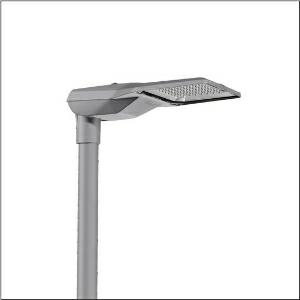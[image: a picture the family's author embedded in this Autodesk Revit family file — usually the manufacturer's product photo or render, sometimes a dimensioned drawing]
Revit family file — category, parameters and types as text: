
# Revit family: streetlight_sl_21_midi___pc-l_5xe3f33s08mb_4952
name_source: partatom
category: Lighting Fixtures
units: mm (PartAtom-declared; Revit-internal decimal feet)

## family parameters
Cut with Voids When Loaded = No
Host = Face
Light Source = No
Part Type = Normal
Room Calculation Point = No
Round Connector Dimension = Use Diameter
Shared = No

## types (1)
- --- (1 x LED, 17390 lm, 136 W, 3000K)
    Apparent Load = 136 VA
    CIE Flux Codes = 38 78 98 100 100
    Color Rendering = 70
    Color Temperature = 3000K
    Default Elevation = 1800 mm
    Description = Streetlight SL 21 midi, mast luminaire, primary light control with lens, of PMMA, primary optical cover: cover, of toughened safety glass, transparent, light distribution: PC-L, light emission: direct distribution, primary light characteristic: asymmetric, left, installation type: side-entry, post-top, LED, High Power LED, rated luminous flux: 17.390lm, luminous efficacy: 128lm/W, light colour: 730, colour temperature: 3000K, control gear: D4i, control: overheat protection, constant luminous flux control, time-dependent luminous flux control, flexible luminous flux parameterisation, pre-setting: logarithmic dimming characteristic, mains connection: 230..240V, AC, 50/60Hz, start of lifetime: 136W, end of service life: 142W, reduction: 61W, luminaire housing, of diecast aluminium, powder-coated, SITECO metallic grey (DB 702S), corrosivity category C5 high according to DIN EN ISO 12944, please order mast flange separately, inclination adjustable: 0°, 5°, 10°, 15°, sealing non-destructively replaceable, multi-level sealing system, length: 644mm, width: 335mm, height: 110mm, mast flange for spigot size: 42mm (side-entry): 5XC10008XM4, 60/48mm (side-entry/post-top): 5XC10108XM2, 76/60mm (side-entry/post-top): 5XC10108XM1, mounting height: 4..8m, Smart Interface above, protection rating (complete): IP66, insulation class (complete): insulation class II (safety insulation), certification: CE, ENEC, ENEC+, VDE, impact resistance: IK10, permissible operating ambient temperature for outdoor applications: -40..+50°C, standard-compliant lighting for roads and squares, packaging unit: 1 piece

Light Distribution: PC-L
    Height = 111 mm
    Lamp = 1 x LED
    Lamp Light Flux = 17390 lm
    Lamp Power = 136 W
    Lamp count = 1
    Length = 644 mm
    Luminous efficacy = 128 lm/W
    Manufacturer = Siteco
    ModVariant = No
    Model = 5XE3F33S08MB
    Number of Poles = 1
    OnlyDefault = Yes
    Power Factor = 1
    Product Name = Streetlight SL 21 midi | PC-L
    Product group = mast luminaire | pylon top
    ProductGroupID = 6100
    Protection Class = Protection class II
    Protection Degree = IP 66
    RLX_Detail_Level = 1
    RLX_Emergency_Light_Flux = 0 lm
    RLX_Emergency_Type = 0
    RLX_Emergency_Type_DB = No
    RlxData = <blob elided: 29501 chars, md5=da359823>
    Socket = socket
    Standby Power = 0 W
    System Light Flux = 17390 lm
    System Power = 136 W
    Type Comments = factory setting: luminous flux: 100 % | dim-lin: 254 | 695 mA
    Type Image = l_1004302.jpg
    URL = http://relux.com
    VarID = @adj_072193
    Voltage = 0 V
    Weight = 0.00 kg
    Width = 336 mm

## geometry (parser evidence)
native form markers: Blend x4, Sweep x11
no freeform markers — native parametric forms only
